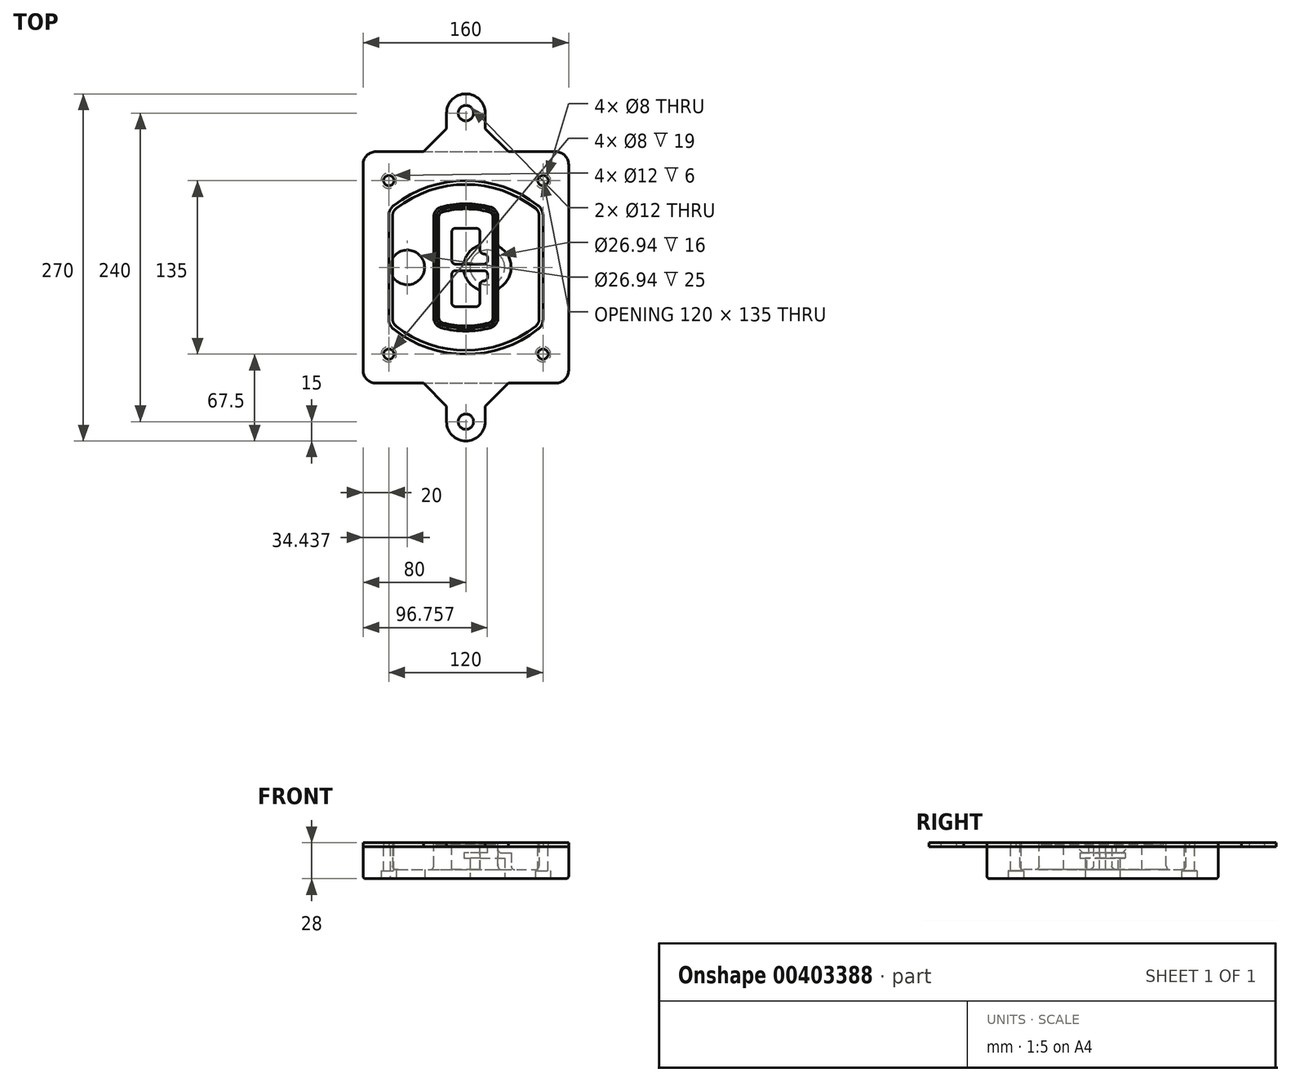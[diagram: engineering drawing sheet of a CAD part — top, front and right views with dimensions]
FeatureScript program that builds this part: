
annotation { "Feature Type Name" : "Feature", "Feature Type Description" : "" }
export const myFeature = defineFeature(function(context is Context, id is Id, definition is map)
    precondition{}
    {
        {
            var Q0;
            Q0=qCreatedBy(makeId("Top.planeOp"),FACE);
            var sketch = newSketch(context, id + "F0", { "sketchPlane" : qUnion([Q0])});
            skPoint(sketch, "E0.rect.middle", {"position": v(0, 0) * mm});
            skLineSegment(sketch, "E1.bottom", {"start": v(-70, -90) * mm, "end": v(70, -90) * mm});
            skLineSegment(sketch, "E1.top", {"start": v(-70, 90) * mm, "end": v(70, 90) * mm});
            skLineSegment(sketch, "E1.left", {"start": v(-80, -80) * mm, "end": v(-80, 80) * mm});
            skLineSegment(sketch, "E1.right", {"start": v(80, -80) * mm, "end": v(80, 80) * mm});
            skLineSegment(sketch, "E2", {"start": v(-80, 90) * mm, "end": v(80, -90) * mm, "construction": true});
            skLineSegment(sketch, "E3", {"start": v(80, 90) * mm, "end": v(-80, -90) * mm, "construction": true});
            skCircle(sketch, "E4", {"center": v(-60, 67.5) * mm, "radius": 4 * mm});
            skCircle(sketch, "E5", {"center": v(60, 67.5) * mm, "radius": 4 * mm});
            skCircle(sketch, "E6", {"center": v(60, -67.5) * mm, "radius": 4 * mm});
            skCircle(sketch, "E7", {"center": v(-60, -67.5) * mm, "radius": 4 * mm});
            skLineSegment(sketch, "E8", {"start": v(-60, 67.5) * mm, "end": v(60, 67.5) * mm, "construction": true});
            skLineSegment(sketch, "E9", {"start": v(60, 67.5) * mm, "end": v(60, -67.5) * mm, "construction": true});
            skLineSegment(sketch, "E10", {"start": v(60, -67.5) * mm, "end": v(-60, -67.5) * mm, "construction": true});
            skLineSegment(sketch, "E11", {"start": v(-60, -67.5) * mm, "end": v(-60, 67.5) * mm, "construction": true});
            skLineSegment(sketch, "E12", {"start": v(-60, 40.3) * mm, "end": v(-60, -40.3) * mm});
            skLineSegment(sketch, "E13", {"start": v(60, 40.3) * mm, "end": v(60, -40.3) * mm});
            skArc(sketch, "E14", {"start": v(56.15, 48.18) * mm, "mid": v(0, 67.5) * mm, "end": v(-56.15, 48.18) * mm});
            skArc(sketch, "E15", {"start": v(-56.15, -48.18) * mm, "mid": v(0, -67.5) * mm, "end": v(56.15, -48.18) * mm});
            skLineSegment(sketch, "E16", {"start": v(-60, 0) * mm, "end": v(60, 0) * mm, "construction": true});
            skPoint(sketch, "E17.visualSharp", {"position": v(-60, -45) * mm});
            skArc(sketch, "E17.filletArc", {"start": v(-60, -40.3) * mm, "mid": v(-58.99, -44.68) * mm, "end": v(-56.15, -48.18) * mm});
            skPoint(sketch, "E18.visualSharp", {"position": v(-60, 45) * mm});
            skArc(sketch, "E18.filletArc", {"start": v(-56.15, 48.18) * mm, "mid": v(-58.99, 44.68) * mm, "end": v(-60, 40.3) * mm});
            skPoint(sketch, "E19.visualSharp", {"position": v(60, 45) * mm});
            skArc(sketch, "E19.filletArc", {"start": v(60, 40.3) * mm, "mid": v(58.99, 44.68) * mm, "end": v(56.15, 48.18) * mm});
            skPoint(sketch, "E20.visualSharp", {"position": v(60, -45) * mm});
            skArc(sketch, "E20.filletArc", {"start": v(56.15, -48.18) * mm, "mid": v(58.99, -44.68) * mm, "end": v(60, -40.3) * mm});
            skPoint(sketch, "E21.visualSharp", {"position": v(-80, 90) * mm});
            skArc(sketch, "E21.filletArc", {"start": v(-70, 90) * mm, "mid": v(-77.07, 87.07) * mm, "end": v(-80, 80) * mm});
            skPoint(sketch, "E22.visualSharp", {"position": v(80, 90) * mm});
            skArc(sketch, "E22.filletArc", {"start": v(80, 80) * mm, "mid": v(77.07, 87.07) * mm, "end": v(70, 90) * mm});
            skPoint(sketch, "E23.visualSharp", {"position": v(80, -90) * mm});
            skArc(sketch, "E23.filletArc", {"start": v(70, -90) * mm, "mid": v(77.07, -87.07) * mm, "end": v(80, -80) * mm});
            skPoint(sketch, "E24.visualSharp", {"position": v(-80, -90) * mm});
            skArc(sketch, "E24.filletArc", {"start": v(-80, -80) * mm, "mid": v(-77.07, -87.07) * mm, "end": v(-70, -90) * mm});
            skArc(sketch, "E25.0", {"start": v(57, 40.3) * mm, "mid": v(56.3, 43.36) * mm, "end": v(54.3, 45.81) * mm});
            skLineSegment(sketch, "E25.1", {"start": v(57, 40.3) * mm, "end": v(57, -40.3) * mm});
            skArc(sketch, "E25.2", {"start": v(54.3, -45.81) * mm, "mid": v(56.3, -43.36) * mm, "end": v(57, -40.3) * mm});
            skArc(sketch, "E25.3", {"start": v(-54.3, -45.81) * mm, "mid": v(0, -64.5) * mm, "end": v(54.3, -45.81) * mm});
            skArc(sketch, "E25.4", {"start": v(-57, -40.3) * mm, "mid": v(-56.3, -43.36) * mm, "end": v(-54.3, -45.81) * mm});
            skArc(sketch, "E25.5", {"start": v(54.3, 45.81) * mm, "mid": v(0, 64.5) * mm, "end": v(-54.3, 45.81) * mm});
            skLineSegment(sketch, "E25.6", {"start": v(-57, 40.3) * mm, "end": v(-57, -40.3) * mm});
            skArc(sketch, "E25.7", {"start": v(-54.3, 45.81) * mm, "mid": v(-56.3, 43.36) * mm, "end": v(-57, 40.3) * mm});
            skArc(sketch, "E26.0", {"start": v(-58.62, 51.33) * mm, "mid": v(-62.58, 46.43) * mm, "end": v(-64, 40.3) * mm});
            skArc(sketch, "E26.1", {"start": v(58.62, 51.33) * mm, "mid": v(0, 71.5) * mm, "end": v(-58.62, 51.33) * mm});
            skArc(sketch, "E26.2", {"start": v(64, 40.3) * mm, "mid": v(62.58, 46.43) * mm, "end": v(58.62, 51.33) * mm});
            skLineSegment(sketch, "E26.3", {"start": v(64, 40.3) * mm, "end": v(64, -40.3) * mm});
            skArc(sketch, "E26.4", {"start": v(58.62, -51.33) * mm, "mid": v(62.58, -46.43) * mm, "end": v(64, -40.3) * mm});
            skLineSegment(sketch, "E26.5", {"start": v(-64, 40.3) * mm, "end": v(-64, -40.3) * mm});
            skArc(sketch, "E26.6", {"start": v(-58.62, -51.33) * mm, "mid": v(0, -71.5) * mm, "end": v(58.62, -51.33) * mm});
            skArc(sketch, "E26.7", {"start": v(-64, -40.3) * mm, "mid": v(-62.58, -46.43) * mm, "end": v(-58.62, -51.33) * mm});
            skSolve(sketch);
        }
        {
            var Q0;
            Q0=makeQuery(id+"F0.imprint","IMPRINT",FACE,{"disambiguationData":[TD([[makeQuery(id+"F0.imprint","IMPRINT",EDGE,{"derivedFrom":sQuery(id+"F0.wireOp",EDGE,"E1.bottom")}),1.0]])]});
            var Q1;
            Q1=makeQuery(id+"F0.imprint","IMPRINT",FACE,{"disambiguationData":[TD([[makeQuery(id+"F0.imprint","IMPRINT",EDGE,{"derivedFrom":sQuery(id+"F0.wireOp",EDGE,"E12")}),1.0]])]});
            var Q2;
            Q2=makeQuery(id+"F0.imprint","IMPRINT",FACE,{"disambiguationData":[TD([[makeQuery(id+"F0.imprint","IMPRINT",EDGE,{"derivedFrom":sQuery(id+"F0.wireOp",EDGE,"E25.0")}),1.0]])]});
            var Q3;
            Q3=makeQuery(id+"F0.imprint","IMPRINT",FACE,{"disambiguationData":[TD([[makeQuery(id+"F0.imprint","IMPRINT",EDGE,{"derivedFrom":sQuery(id+"F0.wireOp",EDGE,"E12")}),-1.0]])]});
            extrude(context, id + "F1", {"entities" : qUnion([Q0, Q1, Q2, Q3]), "oppositeDirection" : true, "depth" : 25 * mm});
        }
        {
            var Q0;
            Q0=makeQuery(id+"F0.imprint","IMPRINT",FACE,{"disambiguationData":[TD([[makeQuery(id+"F0.imprint","IMPRINT",EDGE,{"derivedFrom":sQuery(id+"F0.wireOp",EDGE,"E12")}),1.0]])]});
            extrude(context, id + "F2", {"entities" : qUnion([Q0]), "operationType" : NewBodyOperationType.ADD, "depth" : 3 * mm});
        }
        {
            var Q0;
            Q0=makeQuery(id+"F0.imprint","IMPRINT",FACE,{"disambiguationData":[TD([[makeQuery(id+"F0.imprint","IMPRINT",EDGE,{"derivedFrom":sQuery(id+"F0.wireOp",EDGE,"E25.0")}),1.0]])]});
            extrude(context, id + "F3", {"entities" : qUnion([Q0]), "operationType" : NewBodyOperationType.REMOVE, "oppositeDirection" : true, "depth" : 18 * mm});
        }
        {
            var Q0;
            Q0=makeQuery(id+"F2.opExtrude","CAP_FACE",FACE,{"disambiguationData":[OSD([sQuery(id+"F0.wireOp",EDGE,"E12"),sQuery(id+"F0.wireOp",EDGE,"E13"),sQuery(id+"F0.wireOp",EDGE,"E14"),sQuery(id+"F0.wireOp",EDGE,"E15"),sQuery(id+"F0.wireOp",EDGE,"E17.filletArc"),sQuery(id+"F0.wireOp",EDGE,"E18.filletArc"),sQuery(id+"F0.wireOp",EDGE,"E19.filletArc"),sQuery(id+"F0.wireOp",EDGE,"E20.filletArc"),sQuery(id+"F0.wireOp",EDGE,"E25.0"),sQuery(id+"F0.wireOp",EDGE,"E25.1"),sQuery(id+"F0.wireOp",EDGE,"E25.2"),sQuery(id+"F0.wireOp",EDGE,"E25.3"),sQuery(id+"F0.wireOp",EDGE,"E25.4"),sQuery(id+"F0.wireOp",EDGE,"E25.5"),sQuery(id+"F0.wireOp",EDGE,"E25.6"),sQuery(id+"F0.wireOp",EDGE,"E25.7")])],"isStart":false});
            var sketch = newSketch(context, id + "F4", { "sketchPlane" : qUnion([Q0])});
            skArc(sketch, "E27.0", {"start": v(-19.08, -46.97) * mm, "mid": v(0, -49.5) * mm, "end": v(19.08, -46.97) * mm});
            skArc(sketch, "E28.0", {"start": v(19.08, 46.97) * mm, "mid": v(0, 49.5) * mm, "end": v(-19.08, 46.97) * mm});
            skLineSegment(sketch, "E29", {"start": v(-25, 39.25) * mm, "end": v(-25, -39.25) * mm});
            skLineSegment(sketch, "E30", {"start": v(25, 39.25) * mm, "end": v(25, -39.25) * mm});
            skLineSegment(sketch, "E31", {"start": v(-25, 45.1) * mm, "end": v(25, 45.1) * mm, "construction": true});
            skLineSegment(sketch, "E32", {"start": v(-25, -45.1) * mm, "end": v(25, -45.1) * mm, "construction": true});
            skPoint(sketch, "E33.visualSharp", {"position": v(-25, 45.1) * mm});
            skArc(sketch, "E33.filletArc", {"start": v(-19.08, 46.97) * mm, "mid": v(-23.35, 44.11) * mm, "end": v(-25, 39.25) * mm});
            skPoint(sketch, "E34.visualSharp", {"position": v(25, 45.1) * mm});
            skArc(sketch, "E34.filletArc", {"start": v(25, 39.25) * mm, "mid": v(23.35, 44.11) * mm, "end": v(19.08, 46.97) * mm});
            skPoint(sketch, "E35.visualSharp", {"position": v(25, -45.1) * mm});
            skArc(sketch, "E35.filletArc", {"start": v(19.08, -46.97) * mm, "mid": v(23.35, -44.11) * mm, "end": v(25, -39.25) * mm});
            skPoint(sketch, "E36.visualSharp", {"position": v(-25, -45.1) * mm});
            skArc(sketch, "E36.filletArc", {"start": v(-25, -39.25) * mm, "mid": v(-23.35, -44.11) * mm, "end": v(-19.08, -46.97) * mm});
            skArc(sketch, "E37.0", {"start": v(54.3, 45.81) * mm, "mid": v(0, 64.5) * mm, "end": v(-54.3, 45.81) * mm});
            skArc(sketch, "E37.1", {"start": v(-54.3, 45.81) * mm, "mid": v(-56.3, 43.36) * mm, "end": v(-57, 40.3) * mm});
            skLineSegment(sketch, "E37.2", {"start": v(-57, 40.3) * mm, "end": v(-57, -40.3) * mm});
            skArc(sketch, "E37.3", {"start": v(-57, -40.3) * mm, "mid": v(-56.3, -43.36) * mm, "end": v(-54.3, -45.81) * mm});
            skArc(sketch, "E37.4", {"start": v(-54.3, -45.81) * mm, "mid": v(0, -64.5) * mm, "end": v(54.3, -45.81) * mm});
            skArc(sketch, "E37.5", {"start": v(54.3, -45.81) * mm, "mid": v(56.3, -43.36) * mm, "end": v(57, -40.3) * mm});
            skLineSegment(sketch, "E37.6", {"start": v(57, 40.3) * mm, "end": v(57, -40.3) * mm});
            skArc(sketch, "E37.7", {"start": v(57, 40.3) * mm, "mid": v(56.3, 43.36) * mm, "end": v(54.3, 45.81) * mm});
            skLineSegment(sketch, "E38.0", {"start": v(23, 39.25) * mm, "end": v(23, -39.25) * mm});
            skArc(sketch, "E38.1", {"start": v(18.56, -45.04) * mm, "mid": v(21.76, -42.9) * mm, "end": v(23, -39.25) * mm});
            skArc(sketch, "E38.2", {"start": v(-18.56, -45.04) * mm, "mid": v(0, -47.5) * mm, "end": v(18.56, -45.04) * mm});
            skArc(sketch, "E38.3", {"start": v(-23, -39.25) * mm, "mid": v(-21.76, -42.9) * mm, "end": v(-18.56, -45.04) * mm});
            skLineSegment(sketch, "E38.4", {"start": v(-23, 39.25) * mm, "end": v(-23, -39.25) * mm});
            skArc(sketch, "E38.5", {"start": v(23, 39.25) * mm, "mid": v(21.76, 42.9) * mm, "end": v(18.56, 45.04) * mm});
            skArc(sketch, "E38.6", {"start": v(-18.56, 45.04) * mm, "mid": v(-21.76, 42.9) * mm, "end": v(-23, 39.25) * mm});
            skArc(sketch, "E38.7", {"start": v(18.56, 45.04) * mm, "mid": v(0, 47.5) * mm, "end": v(-18.56, 45.04) * mm});
            skArc(sketch, "E39.0", {"start": v(21, 39.25) * mm, "mid": v(20.18, 41.68) * mm, "end": v(18.04, 43.1) * mm});
            skLineSegment(sketch, "E39.1", {"start": v(21, 39.25) * mm, "end": v(21, -39.25) * mm});
            skArc(sketch, "E39.2", {"start": v(18.04, -43.1) * mm, "mid": v(20.18, -41.68) * mm, "end": v(21, -39.25) * mm});
            skArc(sketch, "E39.3", {"start": v(-18.04, -43.1) * mm, "mid": v(0, -45.5) * mm, "end": v(18.04, -43.1) * mm});
            skArc(sketch, "E39.4", {"start": v(-21, -39.25) * mm, "mid": v(-20.18, -41.68) * mm, "end": v(-18.04, -43.1) * mm});
            skArc(sketch, "E39.5", {"start": v(18.04, 43.1) * mm, "mid": v(0, 45.5) * mm, "end": v(-18.04, 43.1) * mm});
            skLineSegment(sketch, "E39.6", {"start": v(-21, 39.25) * mm, "end": v(-21, -39.25) * mm});
            skArc(sketch, "E39.7", {"start": v(-18.04, 43.1) * mm, "mid": v(-20.18, 41.68) * mm, "end": v(-21, 39.25) * mm});
            skLineSegment(sketch, "E40", {"start": v(-25, 0) * mm, "end": v(25, 0) * mm, "construction": true});
            skLineSegment(sketch, "E41", {"start": v(-11, 5.5) * mm, "end": v(-11, 27.5) * mm});
            skLineSegment(sketch, "E42", {"start": v(-8, 30.5) * mm, "end": v(8, 30.5) * mm});
            skLineSegment(sketch, "E43", {"start": v(11, 27.5) * mm, "end": v(11, 13.5) * mm});
            skLineSegment(sketch, "E44", {"start": v(14, 10.5) * mm, "end": v(14, 10.5) * mm});
            skLineSegment(sketch, "E45", {"start": v(17, 7.5) * mm, "end": v(17, 5.5) * mm});
            skLineSegment(sketch, "E46", {"start": v(14, 2.5) * mm, "end": v(-8, 2.5) * mm});
            skPoint(sketch, "E47.visualSharp", {"position": v(-11, 30.5) * mm});
            skArc(sketch, "E47.filletArc", {"start": v(-8, 30.5) * mm, "mid": v(-10.12, 29.62) * mm, "end": v(-11, 27.5) * mm});
            skPoint(sketch, "E48.visualSharp", {"position": v(11, 30.5) * mm});
            skArc(sketch, "E48.filletArc", {"start": v(11, 27.5) * mm, "mid": v(10.12, 29.62) * mm, "end": v(8, 30.5) * mm});
            skPoint(sketch, "E49.visualSharp", {"position": v(11, 10.5) * mm});
            skArc(sketch, "E49.filletArc", {"start": v(11, 13.5) * mm, "mid": v(11.88, 11.38) * mm, "end": v(14, 10.5) * mm});
            skPoint(sketch, "E50.visualSharp", {"position": v(17, 10.5) * mm});
            skArc(sketch, "E50.filletArc", {"start": v(17, 7.5) * mm, "mid": v(16.12, 9.62) * mm, "end": v(14, 10.5) * mm});
            skPoint(sketch, "E51.visualSharp", {"position": v(17, 2.5) * mm});
            skArc(sketch, "E51.filletArc", {"start": v(14, 2.5) * mm, "mid": v(16.12, 3.38) * mm, "end": v(17, 5.5) * mm});
            skPoint(sketch, "E52.visualSharp", {"position": v(-11, 2.5) * mm});
            skArc(sketch, "E52.filletArc", {"start": v(-11, 5.5) * mm, "mid": v(-10.12, 3.38) * mm, "end": v(-8, 2.5) * mm});
            skLineSegment(sketch, "E53.0.MirrorCS", {"start": v(14, -2.5) * mm, "end": v(-8, -2.5) * mm});
            skArc(sketch, "E54.0.MirrorCS", {"start": v(-11, -5.5) * mm, "mid": v(-10.12, -3.38) * mm, "end": v(-8, -2.5) * mm});
            skLineSegment(sketch, "E55.0.MirrorCS", {"start": v(-11, -5.5) * mm, "end": v(-11, -27.5) * mm});
            skArc(sketch, "E56.0.MirrorCS", {"start": v(-8, -30.5) * mm, "mid": v(-10.12, -29.62) * mm, "end": v(-11, -27.5) * mm});
            skLineSegment(sketch, "E57.0.MirrorCS", {"start": v(-8, -30.5) * mm, "end": v(8, -30.5) * mm});
            skArc(sketch, "E58.0.MirrorCS", {"start": v(11, -27.5) * mm, "mid": v(10.12, -29.62) * mm, "end": v(8, -30.5) * mm});
            skLineSegment(sketch, "E59.0.MirrorCS", {"start": v(11, -27.5) * mm, "end": v(11, -13.5) * mm});
            skArc(sketch, "E60.0.MirrorCS", {"start": v(11, -13.5) * mm, "mid": v(11.88, -11.38) * mm, "end": v(14, -10.5) * mm});
            skArc(sketch, "E61.0.MirrorCS", {"start": v(17, -7.5) * mm, "mid": v(16.12, -9.62) * mm, "end": v(14, -10.5) * mm});
            skLineSegment(sketch, "E62.0.MirrorCS", {"start": v(17, -7.5) * mm, "end": v(17, -5.5) * mm});
            skArc(sketch, "E63.0.MirrorCS", {"start": v(14, -2.5) * mm, "mid": v(16.12, -3.38) * mm, "end": v(17, -5.5) * mm});
            skSolve(sketch);
        }
        {
            var Q0;
            Q0=makeQuery(id+"F4.imprint","IMPRINT",FACE,{"disambiguationData":[TD([[makeQuery(id+"F4.imprint","IMPRINT",EDGE,{"derivedFrom":sQuery(id+"F4.wireOp",EDGE,"E27.0")}),1.0]])]});
            var Q1;
            Q1=makeQuery(id+"F4.imprint","IMPRINT",FACE,{"disambiguationData":[TD([[makeQuery(id+"F4.imprint","IMPRINT",EDGE,{"derivedFrom":sQuery(id+"F4.wireOp",EDGE,"E38.0")}),-1.0]])]});
            var Q2;
            Q2=makeQuery(id+"F4.imprint","IMPRINT",FACE,{"disambiguationData":[TD([[makeQuery(id+"F4.imprint","IMPRINT",EDGE,{"derivedFrom":sQuery(id+"F4.wireOp",EDGE,"E39.0")}),1.0]])]});
            extrude(context, id + "F5", {"entities" : qUnion([Q0, Q1, Q2]), "operationType" : NewBodyOperationType.ADD, "endBound" : BoundingType.UP_TO_NEXT, "oppositeDirection" : true, "depth" : 25 * mm});
        }
        {
            var Q0;
            Q0=makeQuery(id+"F4.imprint","IMPRINT",FACE,{"disambiguationData":[TD([[makeQuery(id+"F4.imprint","IMPRINT",EDGE,{"derivedFrom":sQuery(id+"F4.wireOp",EDGE,"E38.0")}),-1.0]])]});
            extrude(context, id + "F6", {"entities" : qUnion([Q0]), "operationType" : NewBodyOperationType.REMOVE, "oppositeDirection" : true, "depth" : 2 * mm});
        }
        {
            var Q0;
            Q0=makeQuery(id+"F1.opExtrude","CAP_FACE",FACE,{"disambiguationData":[OSD([sQuery(id+"F0.wireOp",EDGE,"E1.bottom"),sQuery(id+"F0.wireOp",EDGE,"E1.top"),sQuery(id+"F0.wireOp",EDGE,"E1.left"),sQuery(id+"F0.wireOp",EDGE,"E1.right"),sQuery(id+"F0.wireOp",EDGE,"E4"),sQuery(id+"F0.wireOp",EDGE,"E5"),sQuery(id+"F0.wireOp",EDGE,"E6"),sQuery(id+"F0.wireOp",EDGE,"E7"),sQuery(id+"F0.wireOp",EDGE,"E21.filletArc"),sQuery(id+"F0.wireOp",EDGE,"E22.filletArc"),sQuery(id+"F0.wireOp",EDGE,"E23.filletArc"),sQuery(id+"F0.wireOp",EDGE,"E24.filletArc")])],"isStart":false});
            var sketch = newSketch(context, id + "F7", { "sketchPlane" : qUnion([Q0])});
            skCircle(sketch, "E64", {"center": v(16.76, 0) * mm, "radius": 13.47 * mm});
            skCircle(sketch, "E65", {"center": v(-45.56, 0) * mm, "radius": 13.47 * mm});
            skLineSegment(sketch, "E66", {"start": v(80, 0) * mm, "end": v(-80, 0) * mm});
            skCircle(sketch, "E67", {"center": v(16.76, 0) * mm, "radius": 18.47 * mm});
            skCircle(sketch, "E68", {"center": v(60, -67.5) * mm, "radius": 6 * mm});
            skCircle(sketch, "E69", {"center": v(-60, -67.5) * mm, "radius": 6 * mm});
            skCircle(sketch, "E70", {"center": v(-60, 67.5) * mm, "radius": 6 * mm});
            skCircle(sketch, "E71", {"center": v(60, 67.5) * mm, "radius": 6 * mm});
            skSolve(sketch);
        }
        {
            var Q0;
            {var subQ1=sQuery(id+"F7.wireOp",EDGE,"E66");var subQ4=sQuery(id+"F7.wireOp",EDGE,"E64");var subQ6=makeQuery(id+"F7.imprint","INTERSECT",VERTEX,{"disambiguationData":[OD(0.0)],"derivedFrom":[subQ4,subQ1]});Q0=makeQuery(id+"F7.imprint","IMPRINT",FACE,{"disambiguationData":[TD([[makeQuery(id+"F7.imprint","IMPRINT",EDGE,{"disambiguationData":[TD([[subQ6,-1.0]])],"derivedFrom":subQ4}),-1.0]])]});}
            var Q1;
            {var subQ0=sQuery(id+"F7.wireOp",EDGE,"E66");var subQ1=sQuery(id+"F7.wireOp",EDGE,"E64");var subQ3=makeQuery(id+"F7.imprint","INTERSECT",VERTEX,{"disambiguationData":[OD(0.0)],"derivedFrom":[subQ1,subQ0]});Q1=makeQuery(id+"F7.imprint","IMPRINT",FACE,{"disambiguationData":[TD([[makeQuery(id+"F7.imprint","IMPRINT",EDGE,{"disambiguationData":[TD([[subQ3,-1.0]])],"derivedFrom":subQ1}),1.0]])]});}
            var Q2;
            {var subQ0=sQuery(id+"F7.wireOp",EDGE,"E66");var subQ1=sQuery(id+"F7.wireOp",EDGE,"E64");var subQ3=makeQuery(id+"F7.imprint","INTERSECT",VERTEX,{"disambiguationData":[OD(0.0)],"derivedFrom":[subQ1,subQ0]});Q2=makeQuery(id+"F7.imprint","IMPRINT",FACE,{"disambiguationData":[TD([[makeQuery(id+"F7.imprint","IMPRINT",EDGE,{"disambiguationData":[TD([[subQ3,1.0]])],"derivedFrom":subQ1}),1.0]])]});}
            var Q3;
            {var subQ1=sQuery(id+"F7.wireOp",EDGE,"E66");var subQ4=sQuery(id+"F7.wireOp",EDGE,"E64");var subQ6=makeQuery(id+"F7.imprint","INTERSECT",VERTEX,{"disambiguationData":[OD(0.0)],"derivedFrom":[subQ4,subQ1]});Q3=makeQuery(id+"F7.imprint","IMPRINT",FACE,{"disambiguationData":[TD([[makeQuery(id+"F7.imprint","IMPRINT",EDGE,{"disambiguationData":[TD([[subQ6,1.0]])],"derivedFrom":subQ4}),-1.0]])]});}
            extrude(context, id + "F8", {"entities" : qUnion([Q0, Q1, Q2, Q3]), "operationType" : NewBodyOperationType.ADD, "oppositeDirection" : true, "depth" : 20 * mm});
        }
        {
            var Q0;
            {var subQ0=sQuery(id+"F7.wireOp",EDGE,"E66");var subQ1=sQuery(id+"F7.wireOp",EDGE,"E64");var subQ3=makeQuery(id+"F7.imprint","INTERSECT",VERTEX,{"disambiguationData":[OD(0.0)],"derivedFrom":[subQ1,subQ0]});Q0=makeQuery(id+"F7.imprint","IMPRINT",FACE,{"disambiguationData":[TD([[makeQuery(id+"F7.imprint","IMPRINT",EDGE,{"disambiguationData":[TD([[subQ3,-1.0]])],"derivedFrom":subQ1}),1.0]])]});}
            var Q1;
            {var subQ0=sQuery(id+"F7.wireOp",EDGE,"E66");var subQ1=sQuery(id+"F7.wireOp",EDGE,"E64");var subQ3=makeQuery(id+"F7.imprint","INTERSECT",VERTEX,{"disambiguationData":[OD(0.0)],"derivedFrom":[subQ1,subQ0]});Q1=makeQuery(id+"F7.imprint","IMPRINT",FACE,{"disambiguationData":[TD([[makeQuery(id+"F7.imprint","IMPRINT",EDGE,{"disambiguationData":[TD([[subQ3,1.0]])],"derivedFrom":subQ1}),1.0]])]});}
            extrude(context, id + "F9", {"entities" : qUnion([Q0, Q1]), "operationType" : NewBodyOperationType.REMOVE, "oppositeDirection" : true, "depth" : 16 * mm});
        }
        {
            var Q0;
            {var subQ0=sQuery(id+"F7.wireOp",EDGE,"E66");var subQ1=sQuery(id+"F7.wireOp",EDGE,"E65");var subQ3=makeQuery(id+"F7.imprint","INTERSECT",VERTEX,{"disambiguationData":[OD(0.0)],"derivedFrom":[subQ1,subQ0]});Q0=makeQuery(id+"F7.imprint","IMPRINT",FACE,{"disambiguationData":[TD([[makeQuery(id+"F7.imprint","IMPRINT",EDGE,{"disambiguationData":[TD([[subQ3,-1.0]])],"derivedFrom":subQ1}),1.0]])]});}
            var Q1;
            {var subQ0=sQuery(id+"F7.wireOp",EDGE,"E66");var subQ1=sQuery(id+"F7.wireOp",EDGE,"E65");var subQ3=makeQuery(id+"F7.imprint","INTERSECT",VERTEX,{"disambiguationData":[OD(0.0)],"derivedFrom":[subQ1,subQ0]});Q1=makeQuery(id+"F7.imprint","IMPRINT",FACE,{"disambiguationData":[TD([[makeQuery(id+"F7.imprint","IMPRINT",EDGE,{"disambiguationData":[TD([[subQ3,1.0]])],"derivedFrom":subQ1}),1.0]])]});}
            extrude(context, id + "F10", {"entities" : qUnion([Q0, Q1]), "operationType" : NewBodyOperationType.REMOVE, "oppositeDirection" : true, "depth" : 25 * mm});
        }
        {
            var Q0;
            Q0=makeQuery(id+"F7.imprint","IMPRINT",FACE,{"disambiguationData":[TD([[makeQuery(id+"F7.imprint","IMPRINT",EDGE,{"derivedFrom":sQuery(id+"F7.wireOp",EDGE,"E68")}),1.0]])]});
            var Q1;
            Q1=makeQuery(id+"F7.imprint","IMPRINT",FACE,{"disambiguationData":[TD([[makeQuery(id+"F7.imprint","IMPRINT",EDGE,{"derivedFrom":makeQuery(id+"F1.opExtrude","CAP_EDGE",EDGE,{"disambiguationData":[OSD([sQuery(id+"F0.wireOp",EDGE,"E5")])],"isStart":false})}),-1.0]])]});
            var Q2;
            Q2=makeQuery(id+"F7.imprint","IMPRINT",FACE,{"disambiguationData":[TD([[makeQuery(id+"F7.imprint","IMPRINT",EDGE,{"derivedFrom":sQuery(id+"F7.wireOp",EDGE,"E69")}),1.0]])]});
            var Q3;
            Q3=makeQuery(id+"F7.imprint","IMPRINT",FACE,{"disambiguationData":[TD([[makeQuery(id+"F7.imprint","IMPRINT",EDGE,{"derivedFrom":makeQuery(id+"F1.opExtrude","CAP_EDGE",EDGE,{"disambiguationData":[OSD([sQuery(id+"F0.wireOp",EDGE,"E4")])],"isStart":false})}),-1.0]])]});
            var Q4;
            Q4=makeQuery(id+"F7.imprint","IMPRINT",FACE,{"disambiguationData":[TD([[makeQuery(id+"F7.imprint","IMPRINT",EDGE,{"derivedFrom":sQuery(id+"F7.wireOp",EDGE,"E70")}),1.0]])]});
            var Q5;
            Q5=makeQuery(id+"F7.imprint","IMPRINT",FACE,{"disambiguationData":[TD([[makeQuery(id+"F7.imprint","IMPRINT",EDGE,{"derivedFrom":makeQuery(id+"F1.opExtrude","CAP_EDGE",EDGE,{"disambiguationData":[OSD([sQuery(id+"F0.wireOp",EDGE,"E7")])],"isStart":false})}),-1.0]])]});
            var Q6;
            Q6=makeQuery(id+"F7.imprint","IMPRINT",FACE,{"disambiguationData":[TD([[makeQuery(id+"F7.imprint","IMPRINT",EDGE,{"derivedFrom":sQuery(id+"F7.wireOp",EDGE,"E71")}),1.0]])]});
            var Q7;
            Q7=makeQuery(id+"F7.imprint","IMPRINT",FACE,{"disambiguationData":[TD([[makeQuery(id+"F7.imprint","IMPRINT",EDGE,{"derivedFrom":makeQuery(id+"F1.opExtrude","CAP_EDGE",EDGE,{"disambiguationData":[OSD([sQuery(id+"F0.wireOp",EDGE,"E6")])],"isStart":false})}),-1.0]])]});
            extrude(context, id + "F11", {"entities" : qUnion([Q0, Q1, Q2, Q3, Q4, Q5, Q6, Q7]), "operationType" : NewBodyOperationType.REMOVE, "oppositeDirection" : true, "depth" : 6 * mm});
        }
        {
            var Q0;
            Q0=makeQuery(id+"F9.boolean.opBoolean","COPY",FACE,{"derivedFrom":makeQuery(id+"F9.opExtrude","CAP_FACE",FACE,{"disambiguationData":[OSD([sQuery(id+"F7.wireOp",EDGE,"E64")])],"isStart":false})});
            var sketch = newSketch(context, id + "F12", { "sketchPlane" : qUnion([Q0])});
            skArc(sketch, "E72.0", {"start": v(11, 17.55) * mm, "mid": v(2.57, 11.82) * mm, "end": v(-1.54, 2.5) * mm});
            skArc(sketch, "E72.1", {"start": v(-1.54, -2.5) * mm, "mid": v(2.57, -11.82) * mm, "end": v(11, -17.55) * mm});
            skLineSegment(sketch, "E73", {"start": v(-1.54, -2.5) * mm, "end": v(14, -2.5) * mm});
            skLineSegment(sketch, "E74.0", {"start": v(14, 2.5) * mm, "end": v(-1.54, 2.5) * mm});
            skArc(sketch, "E74.1", {"start": v(14, 2.5) * mm, "mid": v(16.12, 3.38) * mm, "end": v(17, 5.5) * mm});
            skLineSegment(sketch, "E74.2", {"start": v(17, 7.5) * mm, "end": v(17, 5.5) * mm});
            skArc(sketch, "E74.3", {"start": v(17, 7.5) * mm, "mid": v(16.12, 9.62) * mm, "end": v(14, 10.5) * mm});
            skArc(sketch, "E74.4", {"start": v(11, 13.5) * mm, "mid": v(11.88, 11.38) * mm, "end": v(14, 10.5) * mm});
            skLineSegment(sketch, "E74.5", {"start": v(11, 17.55) * mm, "end": v(11, 13.5) * mm});
            skLineSegment(sketch, "E74.7", {"start": v(14, -2.5) * mm, "end": v(-1.54, -2.5) * mm});
            skArc(sketch, "E74.8", {"start": v(14, -2.5) * mm, "mid": v(16.12, -3.38) * mm, "end": v(17, -5.5) * mm});
            skLineSegment(sketch, "E74.9", {"start": v(17, -7.5) * mm, "end": v(17, -5.5) * mm});
            skArc(sketch, "E74.10", {"start": v(17, -7.5) * mm, "mid": v(16.12, -9.62) * mm, "end": v(14, -10.5) * mm});
            skArc(sketch, "E74.11", {"start": v(11, -13.5) * mm, "mid": v(11.88, -11.38) * mm, "end": v(14, -10.5) * mm});
            skLineSegment(sketch, "E74.12", {"start": v(11, -17.55) * mm, "end": v(11, -13.5) * mm});
            skPoint(sketch, "E75.orphan", {"position": v(11, -27.5) * mm});
            skPoint(sketch, "E76.orphan", {"position": v(-8, -2.5) * mm});
            skPoint(sketch, "E77.orphan", {"position": v(-8, 2.5) * mm});
            skPoint(sketch, "E78.orphan", {"position": v(11, 27.5) * mm});
            skSolve(sketch);
        }
        {
            var Q0;
            {var subQ7=sQuery(id+"F12.wireOp",EDGE,"E72.0");var subQ14=sQuery(id+"F12.wireOp",EDGE,"E72.1");var subQ16=sQuery(id+"F12.wireOp",EDGE,"E74.1");var subQ18=sQuery(id+"F12.wireOp",EDGE,"E74.8");Q0=qUnion([makeQuery(id+"F12.imprint","IMPRINT",FACE,{"disambiguationData":[TD([[makeQuery(id+"F12.imprint","IMPRINT",EDGE,{"derivedFrom":subQ7}),1.0]])]}),makeQuery(id+"F12.imprint","IMPRINT",FACE,{"disambiguationData":[TD([[makeQuery(id+"F12.imprint","IMPRINT",EDGE,{"derivedFrom":subQ14}),1.0]])]}),makeQuery(id+"F12.imprint","IMPRINT",FACE,{"disambiguationData":[TD([[makeQuery(id+"F12.imprint","IMPRINT",EDGE,{"derivedFrom":subQ16}),1.0]])]}),makeQuery(id+"F12.imprint","IMPRINT",FACE,{"disambiguationData":[TD([[makeQuery(id+"F12.imprint","IMPRINT",EDGE,{"derivedFrom":subQ18}),-1.0]])]})]);}
            var Q1;
            Q1=makeQuery(id+"F5.boolean.opBoolean","SPLIT",FACE,{"disambiguationData":[TD([makeQuery(id+"F5.opExtrude","SWEPT_FACE",FACE,{"disambiguationData":[OSD([sQuery(id+"F4.wireOp",EDGE,"E41")])]})])],"derivedFrom":makeQuery(id+"F3.boolean.opBoolean","COPY",FACE,{"derivedFrom":makeQuery(id+"F3.opExtrude","CAP_FACE",FACE,{"disambiguationData":[OSD([sQuery(id+"F0.wireOp",EDGE,"E25.0"),sQuery(id+"F0.wireOp",EDGE,"E25.1"),sQuery(id+"F0.wireOp",EDGE,"E25.2"),sQuery(id+"F0.wireOp",EDGE,"E25.3"),sQuery(id+"F0.wireOp",EDGE,"E25.4"),sQuery(id+"F0.wireOp",EDGE,"E25.5"),sQuery(id+"F0.wireOp",EDGE,"E25.6"),sQuery(id+"F0.wireOp",EDGE,"E25.7")])],"isStart":false})})});
            extrude(context, id + "F13", {"entities" : qUnion([Q0]), "operationType" : NewBodyOperationType.REMOVE, "endBound" : BoundingType.UP_TO_SURFACE, "endBoundEntityFace" : qUnion([Q1]), "depth" : 25 * mm});
        }
        {
            var Q0;
            Q0=makeQuery(id+"F3.boolean.opBoolean","COPY",EDGE,{"derivedFrom":makeQuery(id+"F3.opExtrude","CAP_EDGE",EDGE,{"disambiguationData":[OSD([sQuery(id+"F0.wireOp",EDGE,"E25.6")])],"isStart":false})});
            var Q1;
            Q1=makeQuery(id+"F8.boolean.opBoolean","INTERSECT",EDGE,{"derivedFrom":[makeQuery(id+"F5.opExtrude","SWEPT_FACE",FACE,{"disambiguationData":[OSD([sQuery(id+"F4.wireOp",EDGE,"E30")])]}),makeQuery(id+"F8.opExtrude","CAP_FACE",FACE,{"disambiguationData":[OSD([sQuery(id+"F7.wireOp",EDGE,"E67")])],"isStart":false})]});
            var Q2;
            Q2=makeQuery(id+"F8.boolean.opBoolean","INTERSECT",EDGE,{"disambiguationData":[OD(1.0)],"derivedFrom":[makeQuery(id+"F5.opExtrude","SWEPT_FACE",FACE,{"disambiguationData":[OSD([sQuery(id+"F4.wireOp",EDGE,"E30")])]}),makeQuery(id+"F8.opExtrude","SWEPT_FACE",FACE,{"disambiguationData":[OSD([sQuery(id+"F7.wireOp",EDGE,"E67")])]})]});
            var Q3;
            {var subQ0=sQuery(id+"F4.wireOp",EDGE,"E30");Q3=makeQuery(id+"F8.boolean.opBoolean","SPLIT",EDGE,{"disambiguationData":[TD([makeQuery(id+"F5.opExtrude","SWEPT_FACE",FACE,{"disambiguationData":[OSD([sQuery(id+"F4.wireOp",EDGE,"E35.filletArc")])]})])],"derivedFrom":makeQuery(id+"F5.opExtrude","CAP_EDGE",EDGE,{"disambiguationData":[OSD([subQ0])],"isStart":false})});}
            var Q4;
            {var subQ0=sQuery(id+"F0.wireOp",EDGE,"E25.7");var subQ1=sQuery(id+"F0.wireOp",EDGE,"E25.1");var subQ2=sQuery(id+"F0.wireOp",EDGE,"E25.6");var subQ3=sQuery(id+"F0.wireOp",EDGE,"E25.5");var subQ4=sQuery(id+"F0.wireOp",EDGE,"E25.4");var subQ5=sQuery(id+"F0.wireOp",EDGE,"E25.0");var subQ6=sQuery(id+"F0.wireOp",EDGE,"E25.2");var subQ7=sQuery(id+"F0.wireOp",EDGE,"E25.3");Q4=makeQuery(id+"F8.boolean.opBoolean","INTERSECT",EDGE,{"derivedFrom":[makeQuery(id+"F5.boolean.opBoolean","SPLIT",FACE,{"disambiguationData":[TD([makeQuery(id+"F2.opExtrude","SWEPT_FACE",FACE,{"disambiguationData":[OSD([subQ5])]})])],"derivedFrom":makeQuery(id+"F3.boolean.opBoolean","COPY",FACE,{"derivedFrom":makeQuery(id+"F3.opExtrude","CAP_FACE",FACE,{"disambiguationData":[OSD([subQ5,subQ1,subQ6,subQ7,subQ4,subQ3,subQ2,subQ0])],"isStart":false})})}),makeQuery(id+"F8.opExtrude","SWEPT_FACE",FACE,{"disambiguationData":[OSD([sQuery(id+"F7.wireOp",EDGE,"E67")])]})]});}
            var Q5;
            Q5=makeQuery(id+"F8.boolean.opBoolean","INTERSECT",EDGE,{"disambiguationData":[OD(0.0)],"derivedFrom":[makeQuery(id+"F5.opExtrude","SWEPT_FACE",FACE,{"disambiguationData":[OSD([sQuery(id+"F4.wireOp",EDGE,"E30")])]}),makeQuery(id+"F8.opExtrude","SWEPT_FACE",FACE,{"disambiguationData":[OSD([sQuery(id+"F7.wireOp",EDGE,"E67")])]})]});
            fillet(context, id + "F14", {"entities" : qUnion([Q0, Q1, Q2, Q3, Q4, Q5]), "radius" : 3 * mm, "tangentPropagation" : true, "allowEdgeOverflow" : false});
        }
        {
            var Q0;
            Q0=makeQuery(id+"F1.opExtrude","CAP_EDGE",EDGE,{"disambiguationData":[OSD([sQuery(id+"F0.wireOp",EDGE,"E1.bottom")])],"isStart":false});
            fillet(context, id + "F15", {"entities" : qUnion([Q0]), "radius" : 2 * mm, "tangentPropagation" : true, "allowEdgeOverflow" : false});
        }
        {
            var Q0;
            {var subQ0=sQuery(id+"F0.wireOp",EDGE,"E21.filletArc");var subQ1=sQuery(id+"F0.wireOp",EDGE,"E7");var subQ2=sQuery(id+"F0.wireOp",EDGE,"E6");var subQ3=sQuery(id+"F0.wireOp",EDGE,"E5");var subQ4=sQuery(id+"F0.wireOp",EDGE,"E4");var subQ5=sQuery(id+"F0.wireOp",EDGE,"E22.filletArc");var subQ6=sQuery(id+"F0.wireOp",EDGE,"E1.bottom");var subQ7=sQuery(id+"F0.wireOp",EDGE,"E1.right");var subQ8=sQuery(id+"F0.wireOp",EDGE,"E1.top");var subQ9=sQuery(id+"F0.wireOp",EDGE,"E1.left");var subQ10=sQuery(id+"F0.wireOp",EDGE,"E23.filletArc");var subQ11=sQuery(id+"F0.wireOp",EDGE,"E24.filletArc");Q0=makeQuery(id+"F2.boolean.opBoolean","SPLIT",FACE,{"disambiguationData":[TD([makeQuery(id+"F1.opExtrude","SWEPT_FACE",FACE,{"disambiguationData":[OSD([subQ6])]})])],"derivedFrom":makeQuery(id+"F1.opExtrude","CAP_FACE",FACE,{"disambiguationData":[OSD([subQ6,subQ8,subQ9,subQ7,subQ4,subQ3,subQ2,subQ1,subQ0,subQ5,subQ10,subQ11])],"isStart":true})});}
            var sketch = newSketch(context, id + "F16", { "sketchPlane" : qUnion([Q0])});
            skLineSegment(sketch, "E79.0.0", {"start": v(70, 90) * mm, "end": v(-70, 90) * mm});
            skArc(sketch, "E79.0.1", {"start": v(-70, 90) * mm, "mid": v(-77.07, 87.07) * mm, "end": v(-80, 80) * mm});
            skLineSegment(sketch, "E79.0.2", {"start": v(-80, 80) * mm, "end": v(-80, -80) * mm});
            skArc(sketch, "E79.0.3", {"start": v(-80, -80) * mm, "mid": v(-77.07, -87.07) * mm, "end": v(-70, -90) * mm});
            skLineSegment(sketch, "E79.0.4", {"start": v(-70, -90) * mm, "end": v(70, -90) * mm});
            skArc(sketch, "E79.0.5", {"start": v(70, -90) * mm, "mid": v(77.07, -87.07) * mm, "end": v(80, -80) * mm});
            skLineSegment(sketch, "E79.0.6", {"start": v(80, -80) * mm, "end": v(80, 80) * mm});
            skArc(sketch, "E79.0.7", {"start": v(80, 80) * mm, "mid": v(77.07, 87.07) * mm, "end": v(70, 90) * mm});
            skCircle(sketch, "E80.0", {"center": v(-60, 67.5) * mm, "radius": 4 * mm});
            skCircle(sketch, "E81.0", {"center": v(-60, -67.5) * mm, "radius": 4 * mm});
            skCircle(sketch, "E82.0", {"center": v(60, -67.5) * mm, "radius": 4 * mm});
            skCircle(sketch, "E83.0", {"center": v(60, 67.5) * mm, "radius": 4 * mm});
            skLineSegment(sketch, "E84.0", {"start": v(60, 40.3) * mm, "end": v(60, -40.3) * mm});
            skArc(sketch, "E85.0", {"start": v(56.15, 48.18) * mm, "mid": v(0, 67.5) * mm, "end": v(-56.15, 48.18) * mm});
            skArc(sketch, "E86.0", {"start": v(60, 40.3) * mm, "mid": v(58.99, 44.68) * mm, "end": v(56.15, 48.18) * mm});
            skArc(sketch, "E87.0", {"start": v(-56.15, 48.18) * mm, "mid": v(-58.99, 44.68) * mm, "end": v(-60, 40.3) * mm});
            skLineSegment(sketch, "E88.0", {"start": v(-60, 40.3) * mm, "end": v(-60, -40.3) * mm});
            skArc(sketch, "E89.0", {"start": v(-60, -40.3) * mm, "mid": v(-58.99, -44.68) * mm, "end": v(-56.15, -48.18) * mm});
            skArc(sketch, "E90.0", {"start": v(-56.15, -48.18) * mm, "mid": v(0, -67.5) * mm, "end": v(56.15, -48.18) * mm});
            skArc(sketch, "E91.0", {"start": v(56.15, -48.18) * mm, "mid": v(58.99, -44.68) * mm, "end": v(60, -40.3) * mm});
            skPoint(sketch, "E92.endSnap0", {"position": v(0, 90) * mm});
            skLineSegment(sketch, "E93", {"start": v(0, 90) * mm, "end": v(0, 120) * mm, "construction": true});
            skCircle(sketch, "E94", {"center": v(0, 120) * mm, "radius": 6 * mm});
            skLineSegment(sketch, "E95", {"start": v(-15, 120) * mm, "end": v(-15, 108) * mm});
            skLineSegment(sketch, "E96", {"start": v(-15, 108) * mm, "end": v(-33, 90) * mm});
            skLineSegment(sketch, "E97.MirrorCS", {"start": v(15, 120) * mm, "end": v(15, 108) * mm});
            skLineSegment(sketch, "E98.MirrorCS", {"start": v(15, 108) * mm, "end": v(33, 90) * mm});
            skArc(sketch, "E99", {"start": v(15, 120) * mm, "mid": v(0, 135) * mm, "end": v(-15, 120) * mm});
            skLineSegment(sketch, "E100", {"start": v(-80, 0) * mm, "end": v(80, 0) * mm, "construction": true});
            skLineSegment(sketch, "E101.MirrorCS", {"start": v(-15, -108) * mm, "end": v(-33, -90) * mm});
            skLineSegment(sketch, "E102.MirrorCS", {"start": v(-15, -120) * mm, "end": v(-15, -108) * mm});
            skArc(sketch, "E103.MirrorCS", {"start": v(15, -120) * mm, "mid": v(0, -135) * mm, "end": v(-15, -120) * mm});
            skLineSegment(sketch, "E104.MirrorCS", {"start": v(15, -120) * mm, "end": v(15, -108) * mm});
            skLineSegment(sketch, "E105.MirrorCS", {"start": v(15, -108) * mm, "end": v(33, -90) * mm});
            skCircle(sketch, "E106.MirrorC", {"center": v(0, -120) * mm, "radius": 6 * mm});
            skLineSegment(sketch, "E107.MirrorCS", {"start": v(0, -90) * mm, "end": v(0, -120) * mm, "construction": true});
            skSolve(sketch);
        }
        {
            var Q0;
            Q0 = qSketchRegion(id + "F16", true);
            var Q1;
            Q1=makeQuery(id+"F2.opExtrude","CAP_FACE",FACE,{"disambiguationData":[OSD([sQuery(id+"F0.wireOp",EDGE,"E12"),sQuery(id+"F0.wireOp",EDGE,"E13"),sQuery(id+"F0.wireOp",EDGE,"E14"),sQuery(id+"F0.wireOp",EDGE,"E15"),sQuery(id+"F0.wireOp",EDGE,"E17.filletArc"),sQuery(id+"F0.wireOp",EDGE,"E18.filletArc"),sQuery(id+"F0.wireOp",EDGE,"E19.filletArc"),sQuery(id+"F0.wireOp",EDGE,"E20.filletArc"),sQuery(id+"F0.wireOp",EDGE,"E25.0"),sQuery(id+"F0.wireOp",EDGE,"E25.1"),sQuery(id+"F0.wireOp",EDGE,"E25.2"),sQuery(id+"F0.wireOp",EDGE,"E25.3"),sQuery(id+"F0.wireOp",EDGE,"E25.4"),sQuery(id+"F0.wireOp",EDGE,"E25.5"),sQuery(id+"F0.wireOp",EDGE,"E25.6"),sQuery(id+"F0.wireOp",EDGE,"E25.7")])],"isStart":false});
            extrude(context, id + "F17", {"entities" : qUnion([Q0]), "endBound" : BoundingType.UP_TO_SURFACE, "endBoundEntityFace" : qUnion([Q1]), "depth" : 25 * mm});
        }
    });
